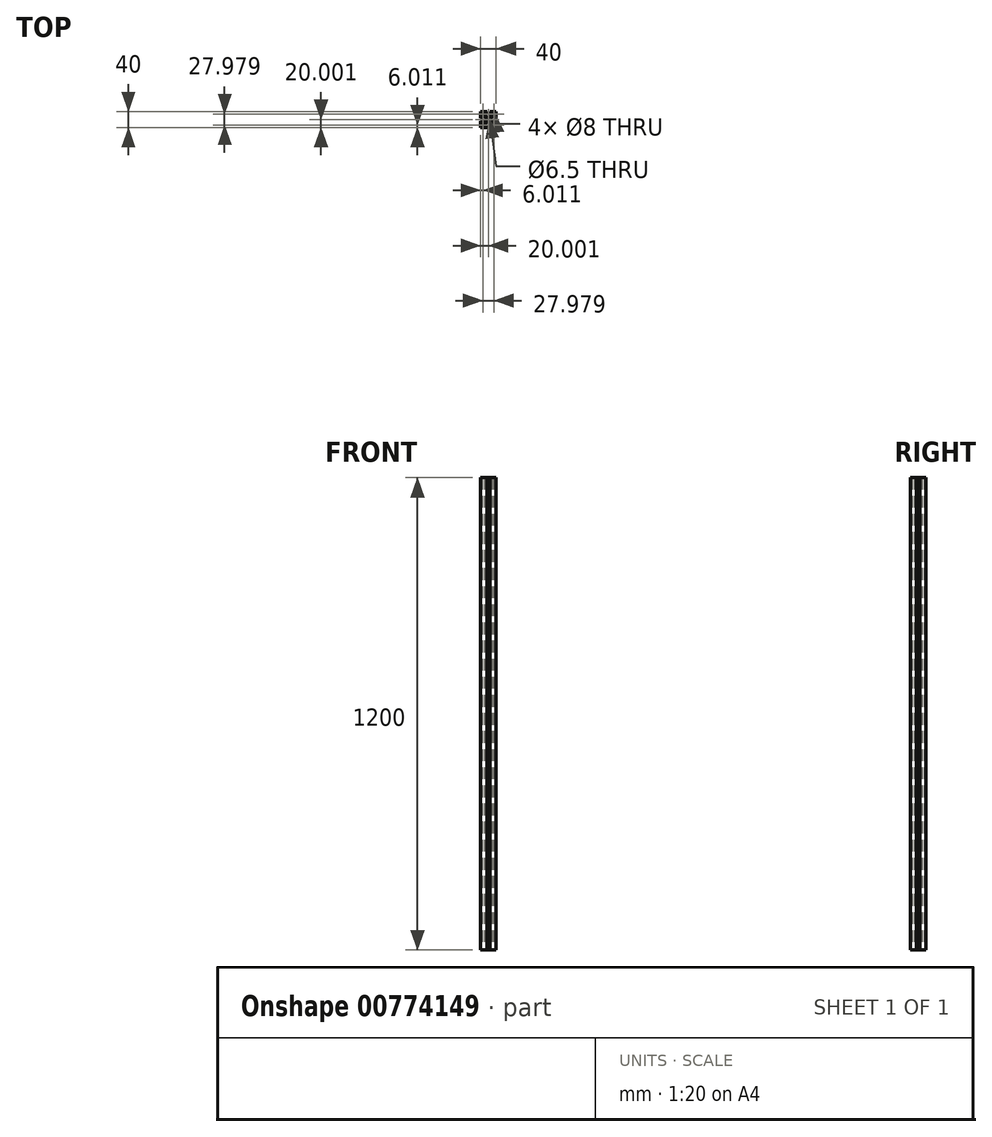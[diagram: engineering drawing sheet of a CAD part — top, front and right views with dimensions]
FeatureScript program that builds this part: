
annotation { "Feature Type Name" : "Feature", "Feature Type Description" : "" }
export const myFeature = defineFeature(function(context is Context, id is Id, definition is map)
    precondition{}
    {
        {
            var Q0;
            Q0=qCreatedBy(makeId("Top.planeOp"),FACE);
            var sketch = newSketch(context, id + "F0", { "sketchPlane" : qUnion([Q0])});
            skCircle(sketch, "E0", {"center": v(5.65, -1.82) * mm, "radius": 4 * mm});
            skCircle(sketch, "E1.MirrorC", {"center": v(33.63, -1.82) * mm, "radius": 4 * mm});
            skCircle(sketch, "E2.MirrorC", {"center": v(33.63, -29.8) * mm, "radius": 4 * mm});
            skCircle(sketch, "E3.MirrorC", {"center": v(5.65, -29.8) * mm, "radius": 4 * mm});
            skCircle(sketch, "E4", {"center": v(19.64, -15.8) * mm, "radius": 3.25 * mm});
            skLineSegment(sketch, "E5", {"start": v(-0.36, 4.2) * mm, "end": v(15.64, 4.2) * mm});
            skLineSegment(sketch, "E6", {"start": v(15.64, 4.2) * mm, "end": v(15.64, 0.2) * mm});
            skLineSegment(sketch, "E7", {"start": v(15.64, 0.2) * mm, "end": v(12.64, 0.2) * mm});
            skLineSegment(sketch, "E8", {"start": v(12.64, 0.2) * mm, "end": v(12.64, -6.8) * mm});
            skLineSegment(sketch, "E9.MirrorCS", {"start": v(26.64, 0.2) * mm, "end": v(26.64, -6.8) * mm});
            skLineSegment(sketch, "E10.MirrorCS", {"start": v(23.64, 0.2) * mm, "end": v(26.64, 0.2) * mm});
            skLineSegment(sketch, "E11.MirrorCS", {"start": v(39.64, 4.2) * mm, "end": v(23.64, 4.2) * mm});
            skLineSegment(sketch, "E12.MirrorCS", {"start": v(23.64, 4.2) * mm, "end": v(23.64, 0.2) * mm});
            skLineSegment(sketch, "E13.MirrorCS", {"start": v(26.64, -31.8) * mm, "end": v(26.64, -24.8) * mm});
            skLineSegment(sketch, "E14.MirrorCS", {"start": v(23.64, -31.8) * mm, "end": v(26.64, -31.8) * mm});
            skLineSegment(sketch, "E15.MirrorCS", {"start": v(23.64, -35.8) * mm, "end": v(23.64, -31.8) * mm});
            skLineSegment(sketch, "E16.MirrorCS", {"start": v(39.64, -35.8) * mm, "end": v(23.64, -35.8) * mm});
            skLineSegment(sketch, "E17.MirrorCS", {"start": v(-0.36, -35.8) * mm, "end": v(15.64, -35.8) * mm});
            skLineSegment(sketch, "E18.MirrorCS", {"start": v(15.64, -35.8) * mm, "end": v(15.64, -31.8) * mm});
            skLineSegment(sketch, "E19.MirrorCS", {"start": v(15.64, -31.8) * mm, "end": v(12.64, -31.8) * mm});
            skLineSegment(sketch, "E20.MirrorCS", {"start": v(12.64, -31.8) * mm, "end": v(12.64, -24.8) * mm});
            skLineSegment(sketch, "E21.MirrorCS", {"start": v(39.64, 4.2) * mm, "end": v(39.64, -11.8) * mm});
            skLineSegment(sketch, "E22.MirrorCS", {"start": v(39.64, -11.8) * mm, "end": v(35.64, -11.8) * mm});
            skLineSegment(sketch, "E23.MirrorCS", {"start": v(35.64, -11.8) * mm, "end": v(35.64, -8.8) * mm});
            skLineSegment(sketch, "E24.MirrorCS", {"start": v(35.64, -8.8) * mm, "end": v(28.64, -8.8) * mm});
            skLineSegment(sketch, "E25.MirrorCS", {"start": v(3.64, -22.8) * mm, "end": v(10.64, -22.8) * mm});
            skLineSegment(sketch, "E26.MirrorCS", {"start": v(-0.36, -19.8) * mm, "end": v(3.64, -19.8) * mm});
            skLineSegment(sketch, "E27.MirrorCS", {"start": v(-0.36, -35.8) * mm, "end": v(-0.36, -19.8) * mm});
            skLineSegment(sketch, "E28.MirrorCS", {"start": v(3.64, -19.8) * mm, "end": v(3.64, -22.8) * mm});
            skLineSegment(sketch, "E29.MirrorCS", {"start": v(39.64, -19.8) * mm, "end": v(35.64, -19.8) * mm});
            skLineSegment(sketch, "E30.MirrorCS", {"start": v(35.64, -19.8) * mm, "end": v(35.64, -22.8) * mm});
            skLineSegment(sketch, "E31.MirrorCS", {"start": v(35.64, -22.8) * mm, "end": v(28.64, -22.8) * mm});
            skLineSegment(sketch, "E32.MirrorCS", {"start": v(3.64, -8.8) * mm, "end": v(10.64, -8.8) * mm});
            skLineSegment(sketch, "E33.MirrorCS", {"start": v(3.64, -11.8) * mm, "end": v(3.64, -8.8) * mm});
            skLineSegment(sketch, "E34.MirrorCS", {"start": v(-0.36, 4.2) * mm, "end": v(-0.36, -11.8) * mm});
            skLineSegment(sketch, "E35.MirrorCS", {"start": v(-0.36, -11.8) * mm, "end": v(3.64, -11.8) * mm});
            skLineSegment(sketch, "E36", {"start": v(39.64, -19.8) * mm, "end": v(39.64, -35.8) * mm});
            skArc(sketch, "E37", {"start": v(12.64, -6.8) * mm, "mid": v(19.64, -9.7) * mm, "end": v(26.64, -6.8) * mm});
            skArc(sketch, "E38", {"start": v(10.64, -8.8) * mm, "mid": v(13.54, -15.8) * mm, "end": v(10.64, -22.8) * mm});
            skArc(sketch, "E39", {"start": v(28.64, -8.8) * mm, "mid": v(25.74, -15.8) * mm, "end": v(28.64, -22.8) * mm});
            skArc(sketch, "E40", {"start": v(26.64, -24.8) * mm, "mid": v(19.64, -21.9) * mm, "end": v(12.64, -24.8) * mm});
            skSolve(sketch);
        }
        {
            var Q0;
            Q0=makeQuery(id+"F0.imprint","IMPRINT",FACE,{"disambiguationData":[TD([[makeQuery(id+"F0.imprint","IMPRINT",EDGE,{"derivedFrom":sQuery(id+"F0.wireOp",EDGE,"E0")}),-1.0]])]});
            extrude(context, id + "F1", {"entities" : qUnion([Q0]), "depth" : 1200 * mm, "offsetDistance" : 25 * mm});
        }
    });
